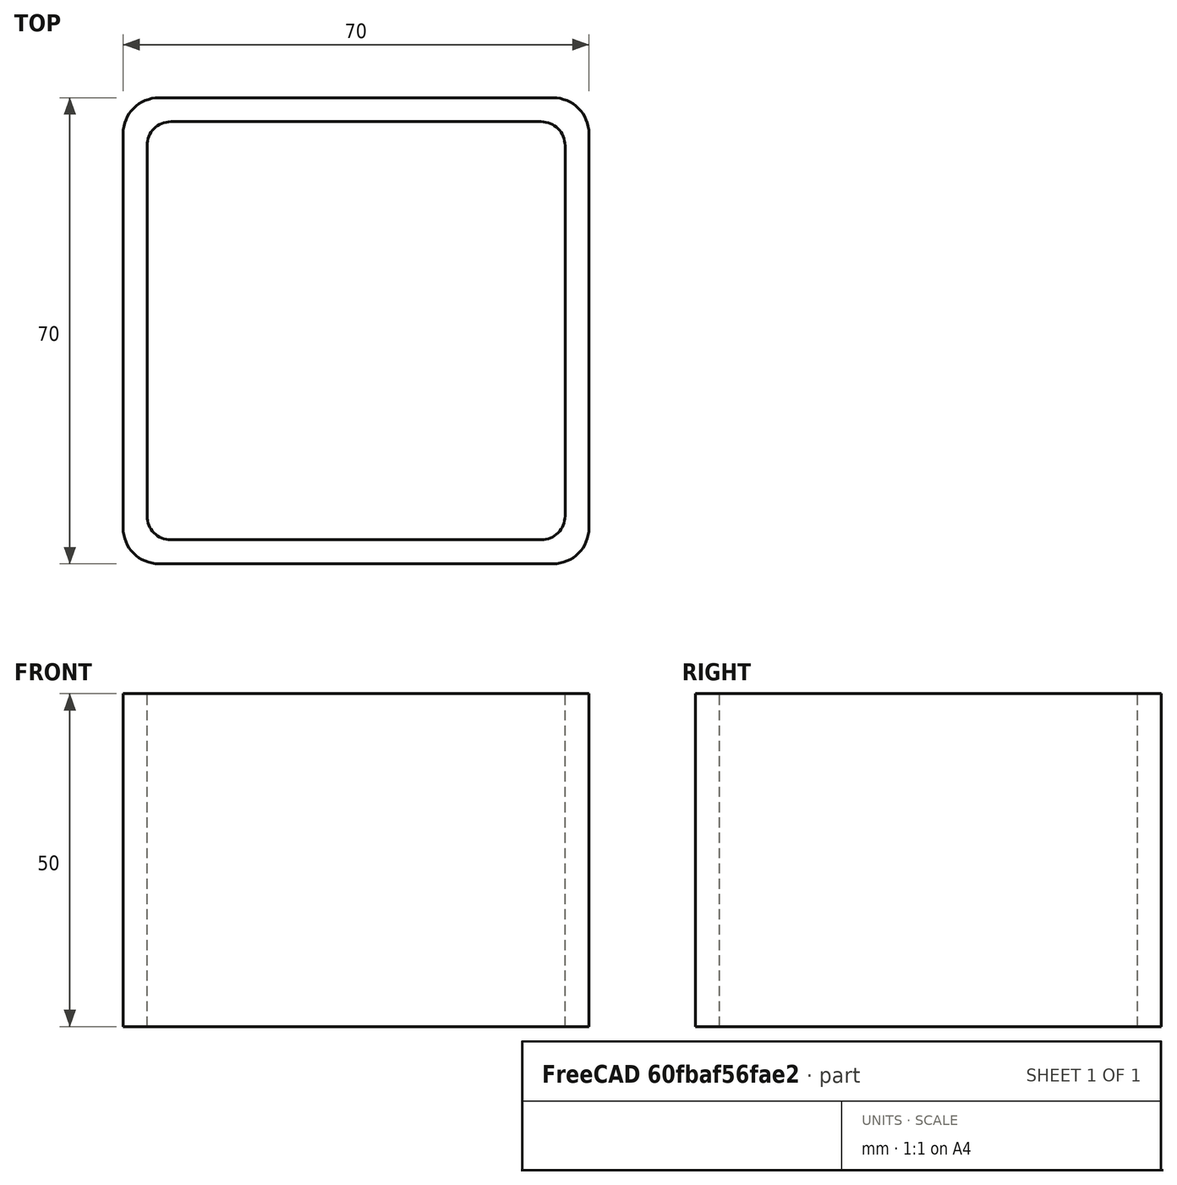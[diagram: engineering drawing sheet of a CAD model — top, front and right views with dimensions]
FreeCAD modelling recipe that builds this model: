
FCSTD DOCUMENT  (FreeCAD 0.15R4671 (Git))
Label: Square hollow section 70x70x3.6 EN10219 S235JRH
License: All rights reserved
LicenseURL: http://en.wikipedia.org/wiki/All_rights_reserved
objects: Sketcher::SketchObject×1, Part::Extrusion×1
note: 2 computed .brp shape members not serialized (recipe doc carries the construction recipe); baked Part::Feature solids carry a one-line shape summary decoded from their .brp

FEATURE [Sketcher::SketchObject] Sketch
  sketch-geometry (16):
    g0: LineSegment StartX=-27.8 StartY=31.4 StartZ=0 EndX=27.8 EndY=31.4 EndZ=0
    g1: LineSegment StartX=31.4 StartY=27.8 StartZ=0 EndX=31.4 EndY=-27.8 EndZ=0
    g2: LineSegment StartX=27.8 StartY=-31.4 StartZ=0 EndX=-27.8 EndY=-31.4 EndZ=0
    g3: LineSegment StartX=-31.4 StartY=-27.8 StartZ=0 EndX=-31.4 EndY=27.8 EndZ=0
    g4: LineSegment StartX=-29.6 StartY=35 StartZ=0 EndX=29.6 EndY=35 EndZ=0
    g5: LineSegment StartX=35 StartY=29.6 StartZ=0 EndX=35 EndY=-29.6 EndZ=0
    g6: LineSegment StartX=29.6 StartY=-35 StartZ=0 EndX=-29.6 EndY=-35 EndZ=0
    g7: LineSegment StartX=-35 StartY=-29.6 StartZ=0 EndX=-35 EndY=29.6 EndZ=0
    g8: ArcOfCircle CenterX=-27.8 CenterY=27.8 CenterZ=0 NormalX=0 NormalY=0 NormalZ=1 Radius=3.6 StartAngle=1.5708 EndAngle=3.14159
    g9: ArcOfCircle CenterX=27.8 CenterY=27.8 CenterZ=0 NormalX=0 NormalY=0 NormalZ=1 Radius=3.6 StartAngle=0 EndAngle=1.5708
    g10: ArcOfCircle CenterX=27.8 CenterY=-27.8 CenterZ=0 NormalX=0 NormalY=0 NormalZ=1 Radius=3.6 StartAngle=4.71239 EndAngle=6.28319
    g11: ArcOfCircle CenterX=-27.8 CenterY=-27.8 CenterZ=0 NormalX=0 NormalY=0 NormalZ=1 Radius=3.6 StartAngle=3.14159 EndAngle=4.71239
    g12: ArcOfCircle CenterX=29.6 CenterY=29.6 CenterZ=0 NormalX=0 NormalY=0 NormalZ=1 Radius=5.4 StartAngle=0 EndAngle=1.5708
    g13: ArcOfCircle CenterX=29.6 CenterY=-29.6 CenterZ=0 NormalX=0 NormalY=0 NormalZ=1 Radius=5.4 StartAngle=4.71239 EndAngle=6.28319
    g14: ArcOfCircle CenterX=-29.6 CenterY=-29.6 CenterZ=0 NormalX=0 NormalY=0 NormalZ=1 Radius=5.4 StartAngle=3.14159 EndAngle=4.71239
    g15: ArcOfCircle CenterX=-29.6 CenterY=29.6 CenterZ=0 NormalX=0 NormalY=0 NormalZ=1 Radius=5.4 StartAngle=1.5708 EndAngle=3.14159
  constraints (36):
    c: Horizontal(g2)
    c: Vertical(g3)
    c: Horizontal(g6)
    c: Vertical(g7)
    c: Tangent(g3,g8) = 1.5708
    c: Tangent(g0,g8) = 1.5708
    c: Tangent(g0,g9) = 1.5708
    c: Tangent(g1,g9) = 1.5708
    c: Tangent(g1,g10) = 1.5708
    c: Tangent(g2,g10) = 1.5708
    c: Tangent(g2,g11) = 1.5708
    c: Tangent(g3,g11) = 1.5708
    c: Tangent(g4,g12) = 1.5708
    c: Tangent(g5,g12) = 1.5708
    c: Tangent(g5,g13) = 1.5708
    c: Tangent(g6,g13) = 1.5708
    c: Tangent(g6,g14) = 1.5708
    c: Tangent(g7,g14) = 1.5708
    c: Tangent(g7,g15) = 1.5708
    c: Tangent(g4,g15) = 1.5708
    c: Equal(g9,g8)
    c: Equal(g9,g11)
    c: Equal(g9,g10)
    c: Equal(g12,g15)
    c: Equal(g12,g14)
    c: Equal(g12,g13)
    c: Symmetric(g4,g6,g-1)
    c: Symmetric(g7,g5,g-2)
    c: DistanceY(g4,g6) = -70
    c: DistanceX(g7,g5) = 70
    c: Symmetric(g3,g1,g-2)
    c: Symmetric(g0,g2,g-1)
    c: DistanceY(g0,g4) = 3.6
    c: DistanceX(g5,g1) = -3.6
    c: Radius(g9) = 3.6
    c: Radius(g12) = 5.4
FEATURE [Part::Extrusion] Extrude  label="Square hollow section 70x70x3.6 EN10219 S235JRH"
  Base = -> Sketch
  Dir = (0,0,50)
  Solid = true
